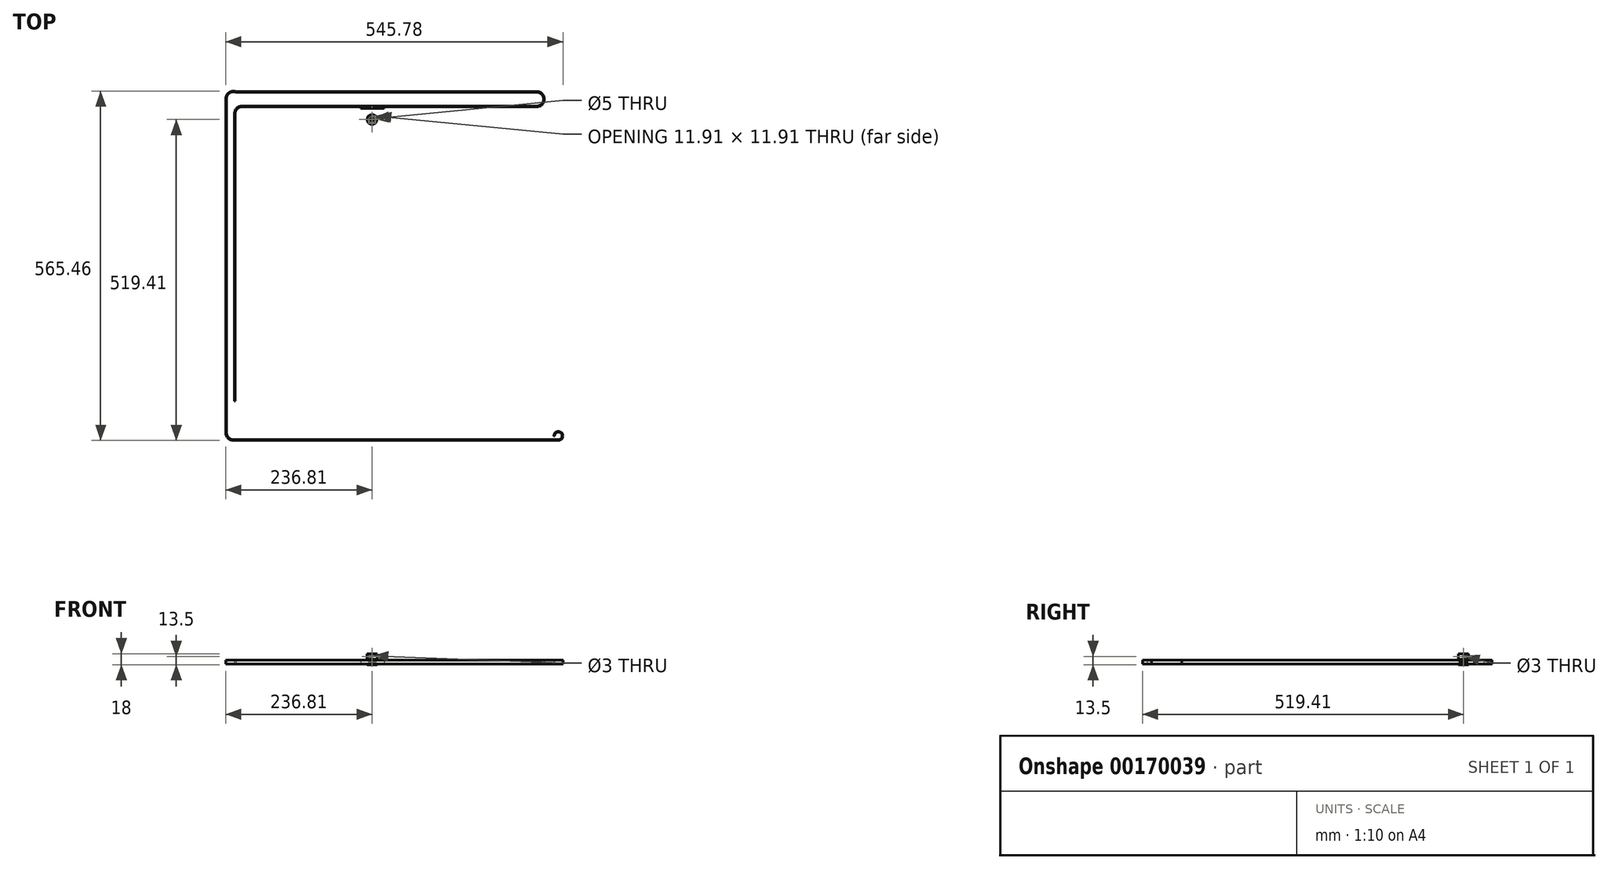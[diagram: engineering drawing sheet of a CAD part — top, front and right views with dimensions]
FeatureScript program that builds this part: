
annotation { "Feature Type Name" : "Feature", "Feature Type Description" : "" }
export const myFeature = defineFeature(function(context is Context, id is Id, definition is map)
    precondition{}
    {
        {
            var Q0;
            Q0=qCreatedBy(makeId("Top.planeOp"),FACE);
            var sketch = newSketch(context, id + "F0", { "sketchPlane" : qUnion([Q0])});
            skLineSegment(sketch, "E0", {"start": v(-19.17, 17.78) * mm, "end": v(-18.17, 17.78) * mm});
            skLineSegment(sketch, "E1", {"start": v(-18.17, 17.78) * mm, "end": v(-18.17, 18.4) * mm});
            skArc(sketch, "E2", {"start": v(-18.67, 18.85) * mm, "mid": v(-18.88, 19.07) * mm, "end": v(-19.17, 19.16) * mm});
            skArc(sketch, "E3", {"start": v(-18.58, 18.54) * mm, "mid": v(-18.61, 18.7) * mm, "end": v(-18.67, 18.85) * mm});
            skArc(sketch, "E4", {"start": v(-18.58, 18.54) * mm, "mid": v(-18.53, 18.44) * mm, "end": v(-18.43, 18.4) * mm});
            skLineSegment(sketch, "E5", {"start": v(-18.43, 18.4) * mm, "end": v(-18.17, 18.4) * mm});
            skArc(sketch, "E6.0.MirrorCS", {"start": v(-19.67, 18.85) * mm, "mid": v(-19.47, 19.07) * mm, "end": v(-19.17, 19.16) * mm});
            skArc(sketch, "E7.0.MirrorCS", {"start": v(-19.76, 18.54) * mm, "mid": v(-19.73, 18.7) * mm, "end": v(-19.67, 18.85) * mm});
            skArc(sketch, "E8.0.MirrorCS", {"start": v(-19.76, 18.54) * mm, "mid": v(-19.81, 18.44) * mm, "end": v(-19.91, 18.4) * mm});
            skLineSegment(sketch, "E9.0.MirrorCS", {"start": v(-19.91, 18.4) * mm, "end": v(-20.17, 18.4) * mm});
            skLineSegment(sketch, "E10.0.MirrorCS", {"start": v(-20.17, 17.78) * mm, "end": v(-20.17, 18.4) * mm});
            skLineSegment(sketch, "E11.0.MirrorCS", {"start": v(-19.17, 17.78) * mm, "end": v(-20.17, 17.78) * mm});
            skLineSegment(sketch, "E12.direction1", {"start": v(-20.17, 17.78) * mm, "end": v(-18.17, 17.78) * mm, "construction": true});
            skLineSegment(sketch, "E13", {"start": v(-20.17, 18.15) * mm, "end": v(-18.17, 18.15) * mm, "construction": true});
            skPoint(sketch, "E14", {"position": v(0, -5.25) * mm});
            skArc(sketch, "E15", {"start": v(0.51, -5.6) * mm, "mid": v(0, -5.25) * mm, "end": v(-0.51, -5.6) * mm});
            skArc(sketch, "E16", {"start": v(-0.51, -5.6) * mm, "mid": v(-0.56, -5.71) * mm, "end": v(-0.59, -5.83) * mm});
            skArc(sketch, "E17", {"start": v(0.59, -5.83) * mm, "mid": v(0.56, -5.71) * mm, "end": v(0.51, -5.6) * mm});
            skArc(sketch, "E18", {"start": v(0.72, -5.96) * mm, "mid": v(0.94, -5.93) * mm, "end": v(1.16, -5.89) * mm});
            skArc(sketch, "E19", {"start": v(0.59, -5.83) * mm, "mid": v(0.66, -5.94) * mm, "end": v(0.8, -5.95) * mm});
            skArc(sketch, "E20", {"start": v(-0.59, -5.83) * mm, "mid": v(-0.66, -5.94) * mm, "end": v(-0.8, -5.95) * mm});
            skArc(sketch, "E21.1.0", {"start": v(2.22, -5.16) * mm, "mid": v(1.62, -5) * mm, "end": v(1.24, -5.48) * mm});
            skPoint(sketch, "E21.1.1", {"position": v(1.62, -5) * mm});
            skArc(sketch, "E21.1.2", {"start": v(1.24, -5.48) * mm, "mid": v(1.23, -5.6) * mm, "end": v(1.24, -5.73) * mm});
            skArc(sketch, "E21.1.3", {"start": v(2.36, -5.37) * mm, "mid": v(2.47, -5.44) * mm, "end": v(2.6, -5.41) * mm});
            skArc(sketch, "E21.1.4", {"start": v(1.24, -5.73) * mm, "mid": v(1.2, -5.85) * mm, "end": v(1.08, -5.9) * mm});
            skArc(sketch, "E21.1.5", {"start": v(2.36, -5.37) * mm, "mid": v(2.3, -5.26) * mm, "end": v(2.22, -5.16) * mm});
            skArc(sketch, "E22.3.2.0", {"start": v(3.7, -4.22) * mm, "mid": v(3.09, -4.25) * mm, "end": v(2.87, -4.83) * mm});
            skPoint(sketch, "E22.4.2.0", {"position": v(3.09, -4.25) * mm});
            skArc(sketch, "E22.5.2.0", {"start": v(2.87, -4.83) * mm, "mid": v(2.9, -4.95) * mm, "end": v(2.95, -5.07) * mm});
            skArc(sketch, "E22.9.2.0", {"start": v(3.9, -4.37) * mm, "mid": v(4.03, -4.41) * mm, "end": v(4.14, -4.35) * mm});
            skArc(sketch, "E22.13.2.0", {"start": v(2.95, -5.07) * mm, "mid": v(2.95, -5.2) * mm, "end": v(2.85, -5.28) * mm});
            skArc(sketch, "E22.17.2.0", {"start": v(3.9, -4.37) * mm, "mid": v(3.81, -4.3) * mm, "end": v(3.7, -4.22) * mm});
            skArc(sketch, "E22.3.3.0", {"start": v(4.83, -2.87) * mm, "mid": v(4.25, -3.09) * mm, "end": v(4.22, -3.7) * mm});
            skPoint(sketch, "E22.4.3.0", {"position": v(4.25, -3.09) * mm});
            skArc(sketch, "E22.5.3.0", {"start": v(4.22, -3.7) * mm, "mid": v(4.3, -3.81) * mm, "end": v(4.37, -3.9) * mm});
            skArc(sketch, "E22.9.3.0", {"start": v(5.07, -2.95) * mm, "mid": v(5.2, -2.95) * mm, "end": v(5.28, -2.85) * mm});
            skArc(sketch, "E22.13.3.0", {"start": v(4.37, -3.9) * mm, "mid": v(4.41, -4.03) * mm, "end": v(4.35, -4.14) * mm});
            skArc(sketch, "E22.17.3.0", {"start": v(5.07, -2.95) * mm, "mid": v(4.95, -2.9) * mm, "end": v(4.83, -2.87) * mm});
            skArc(sketch, "E22.3.4.0", {"start": v(5.48, -1.24) * mm, "mid": v(5, -1.62) * mm, "end": v(5.16, -2.22) * mm});
            skPoint(sketch, "E22.4.4.0", {"position": v(5, -1.62) * mm});
            skArc(sketch, "E22.5.4.0", {"start": v(5.16, -2.22) * mm, "mid": v(5.26, -2.3) * mm, "end": v(5.37, -2.36) * mm});
            skArc(sketch, "E22.9.4.0", {"start": v(5.73, -1.24) * mm, "mid": v(5.85, -1.2) * mm, "end": v(5.9, -1.08) * mm});
            skArc(sketch, "E22.13.4.0", {"start": v(5.37, -2.36) * mm, "mid": v(5.44, -2.47) * mm, "end": v(5.41, -2.6) * mm});
            skArc(sketch, "E22.17.4.0", {"start": v(5.73, -1.24) * mm, "mid": v(5.6, -1.23) * mm, "end": v(5.48, -1.24) * mm});
            skArc(sketch, "E22.3.5.0", {"start": v(5.6, 0.51) * mm, "mid": v(5.25, 0) * mm, "end": v(5.6, -0.51) * mm});
            skPoint(sketch, "E22.4.5.0", {"position": v(5.25, 0) * mm});
            skArc(sketch, "E22.5.5.0", {"start": v(5.6, -0.51) * mm, "mid": v(5.71, -0.56) * mm, "end": v(5.83, -0.59) * mm});
            skArc(sketch, "E22.9.5.0", {"start": v(5.83, 0.59) * mm, "mid": v(5.94, 0.66) * mm, "end": v(5.95, 0.8) * mm});
            skArc(sketch, "E22.13.5.0", {"start": v(5.83, -0.59) * mm, "mid": v(5.94, -0.66) * mm, "end": v(5.95, -0.8) * mm});
            skArc(sketch, "E22.17.5.0", {"start": v(5.83, 0.59) * mm, "mid": v(5.71, 0.56) * mm, "end": v(5.6, 0.51) * mm});
            skArc(sketch, "E22.3.6.0", {"start": v(5.16, 2.22) * mm, "mid": v(5, 1.62) * mm, "end": v(5.48, 1.24) * mm});
            skPoint(sketch, "E22.4.6.0", {"position": v(5, 1.62) * mm});
            skArc(sketch, "E22.5.6.0", {"start": v(5.48, 1.24) * mm, "mid": v(5.6, 1.23) * mm, "end": v(5.73, 1.24) * mm});
            skArc(sketch, "E22.9.6.0", {"start": v(5.37, 2.36) * mm, "mid": v(5.44, 2.47) * mm, "end": v(5.41, 2.6) * mm});
            skArc(sketch, "E22.13.6.0", {"start": v(5.73, 1.24) * mm, "mid": v(5.85, 1.2) * mm, "end": v(5.9, 1.08) * mm});
            skArc(sketch, "E22.17.6.0", {"start": v(5.37, 2.36) * mm, "mid": v(5.26, 2.3) * mm, "end": v(5.16, 2.22) * mm});
            skArc(sketch, "E22.3.7.0", {"start": v(4.22, 3.7) * mm, "mid": v(4.25, 3.09) * mm, "end": v(4.83, 2.87) * mm});
            skPoint(sketch, "E22.4.7.0", {"position": v(4.25, 3.09) * mm});
            skArc(sketch, "E22.5.7.0", {"start": v(4.83, 2.87) * mm, "mid": v(4.95, 2.9) * mm, "end": v(5.07, 2.95) * mm});
            skArc(sketch, "E22.9.7.0", {"start": v(4.37, 3.9) * mm, "mid": v(4.41, 4.03) * mm, "end": v(4.35, 4.14) * mm});
            skArc(sketch, "E22.13.7.0", {"start": v(5.07, 2.95) * mm, "mid": v(5.2, 2.95) * mm, "end": v(5.28, 2.85) * mm});
            skArc(sketch, "E22.17.7.0", {"start": v(4.37, 3.9) * mm, "mid": v(4.3, 3.81) * mm, "end": v(4.22, 3.7) * mm});
            skArc(sketch, "E22.3.8.0", {"start": v(2.87, 4.83) * mm, "mid": v(3.09, 4.25) * mm, "end": v(3.7, 4.22) * mm});
            skPoint(sketch, "E22.4.8.0", {"position": v(3.09, 4.25) * mm});
            skArc(sketch, "E22.5.8.0", {"start": v(3.7, 4.22) * mm, "mid": v(3.81, 4.3) * mm, "end": v(3.9, 4.37) * mm});
            skArc(sketch, "E22.9.8.0", {"start": v(2.95, 5.07) * mm, "mid": v(2.95, 5.2) * mm, "end": v(2.85, 5.28) * mm});
            skArc(sketch, "E22.13.8.0", {"start": v(3.9, 4.37) * mm, "mid": v(4.03, 4.41) * mm, "end": v(4.14, 4.35) * mm});
            skArc(sketch, "E22.17.8.0", {"start": v(2.95, 5.07) * mm, "mid": v(2.9, 4.95) * mm, "end": v(2.87, 4.83) * mm});
            skArc(sketch, "E22.3.9.0", {"start": v(1.24, 5.48) * mm, "mid": v(1.62, 5) * mm, "end": v(2.22, 5.16) * mm});
            skPoint(sketch, "E22.4.9.0", {"position": v(1.62, 5) * mm});
            skArc(sketch, "E22.5.9.0", {"start": v(2.22, 5.16) * mm, "mid": v(2.3, 5.26) * mm, "end": v(2.36, 5.37) * mm});
            skArc(sketch, "E22.9.9.0", {"start": v(1.24, 5.73) * mm, "mid": v(1.2, 5.85) * mm, "end": v(1.08, 5.9) * mm});
            skArc(sketch, "E22.13.9.0", {"start": v(2.36, 5.37) * mm, "mid": v(2.47, 5.44) * mm, "end": v(2.6, 5.41) * mm});
            skArc(sketch, "E22.17.9.0", {"start": v(1.24, 5.73) * mm, "mid": v(1.23, 5.6) * mm, "end": v(1.24, 5.48) * mm});
            skArc(sketch, "E22.3.10.0", {"start": v(-0.51, 5.6) * mm, "mid": v(0, 5.25) * mm, "end": v(0.51, 5.6) * mm});
            skPoint(sketch, "E22.4.10.0", {"position": v(0, 5.25) * mm});
            skArc(sketch, "E22.5.10.0", {"start": v(0.51, 5.6) * mm, "mid": v(0.56, 5.71) * mm, "end": v(0.59, 5.83) * mm});
            skArc(sketch, "E22.9.10.0", {"start": v(-0.59, 5.83) * mm, "mid": v(-0.66, 5.94) * mm, "end": v(-0.8, 5.95) * mm});
            skArc(sketch, "E22.13.10.0", {"start": v(0.59, 5.83) * mm, "mid": v(0.66, 5.94) * mm, "end": v(0.8, 5.95) * mm});
            skArc(sketch, "E22.17.10.0", {"start": v(-0.59, 5.83) * mm, "mid": v(-0.56, 5.71) * mm, "end": v(-0.51, 5.6) * mm});
            skArc(sketch, "E22.3.11.0", {"start": v(-2.22, 5.16) * mm, "mid": v(-1.62, 5) * mm, "end": v(-1.24, 5.48) * mm});
            skPoint(sketch, "E22.4.11.0", {"position": v(-1.62, 5) * mm});
            skArc(sketch, "E22.5.11.0", {"start": v(-1.24, 5.48) * mm, "mid": v(-1.23, 5.6) * mm, "end": v(-1.24, 5.73) * mm});
            skArc(sketch, "E22.9.11.0", {"start": v(-2.36, 5.37) * mm, "mid": v(-2.47, 5.44) * mm, "end": v(-2.6, 5.41) * mm});
            skArc(sketch, "E22.13.11.0", {"start": v(-1.24, 5.73) * mm, "mid": v(-1.2, 5.85) * mm, "end": v(-1.08, 5.9) * mm});
            skArc(sketch, "E22.17.11.0", {"start": v(-2.36, 5.37) * mm, "mid": v(-2.3, 5.26) * mm, "end": v(-2.22, 5.16) * mm});
            skArc(sketch, "E22.3.12.0", {"start": v(-3.7, 4.22) * mm, "mid": v(-3.09, 4.25) * mm, "end": v(-2.87, 4.83) * mm});
            skPoint(sketch, "E22.4.12.0", {"position": v(-3.09, 4.25) * mm});
            skArc(sketch, "E22.5.12.0", {"start": v(-2.87, 4.83) * mm, "mid": v(-2.9, 4.95) * mm, "end": v(-2.95, 5.07) * mm});
            skArc(sketch, "E22.9.12.0", {"start": v(-3.9, 4.37) * mm, "mid": v(-4.03, 4.41) * mm, "end": v(-4.14, 4.35) * mm});
            skArc(sketch, "E22.13.12.0", {"start": v(-2.95, 5.07) * mm, "mid": v(-2.95, 5.2) * mm, "end": v(-2.85, 5.28) * mm});
            skArc(sketch, "E22.17.12.0", {"start": v(-3.9, 4.37) * mm, "mid": v(-3.81, 4.3) * mm, "end": v(-3.7, 4.22) * mm});
            skArc(sketch, "E22.3.13.0", {"start": v(-4.83, 2.87) * mm, "mid": v(-4.25, 3.09) * mm, "end": v(-4.22, 3.7) * mm});
            skPoint(sketch, "E22.4.13.0", {"position": v(-4.25, 3.09) * mm});
            skArc(sketch, "E22.5.13.0", {"start": v(-4.22, 3.7) * mm, "mid": v(-4.3, 3.81) * mm, "end": v(-4.37, 3.9) * mm});
            skArc(sketch, "E22.9.13.0", {"start": v(-5.07, 2.95) * mm, "mid": v(-5.2, 2.95) * mm, "end": v(-5.28, 2.85) * mm});
            skArc(sketch, "E22.13.13.0", {"start": v(-4.37, 3.9) * mm, "mid": v(-4.41, 4.03) * mm, "end": v(-4.35, 4.14) * mm});
            skArc(sketch, "E22.17.13.0", {"start": v(-5.07, 2.95) * mm, "mid": v(-4.95, 2.9) * mm, "end": v(-4.83, 2.87) * mm});
            skArc(sketch, "E22.3.14.0", {"start": v(-5.48, 1.24) * mm, "mid": v(-5, 1.62) * mm, "end": v(-5.16, 2.22) * mm});
            skPoint(sketch, "E22.4.14.0", {"position": v(-5, 1.62) * mm});
            skArc(sketch, "E22.5.14.0", {"start": v(-5.16, 2.22) * mm, "mid": v(-5.26, 2.3) * mm, "end": v(-5.37, 2.36) * mm});
            skArc(sketch, "E22.9.14.0", {"start": v(-5.73, 1.24) * mm, "mid": v(-5.85, 1.2) * mm, "end": v(-5.9, 1.08) * mm});
            skArc(sketch, "E22.13.14.0", {"start": v(-5.37, 2.36) * mm, "mid": v(-5.44, 2.47) * mm, "end": v(-5.41, 2.6) * mm});
            skArc(sketch, "E22.17.14.0", {"start": v(-5.73, 1.24) * mm, "mid": v(-5.6, 1.23) * mm, "end": v(-5.48, 1.24) * mm});
            skArc(sketch, "E22.3.15.0", {"start": v(-5.6, -0.51) * mm, "mid": v(-5.25, 0) * mm, "end": v(-5.6, 0.51) * mm});
            skPoint(sketch, "E22.4.15.0", {"position": v(-5.25, 0) * mm});
            skArc(sketch, "E22.5.15.0", {"start": v(-5.6, 0.51) * mm, "mid": v(-5.71, 0.56) * mm, "end": v(-5.83, 0.59) * mm});
            skArc(sketch, "E22.9.15.0", {"start": v(-5.83, -0.59) * mm, "mid": v(-5.94, -0.66) * mm, "end": v(-5.95, -0.8) * mm});
            skArc(sketch, "E22.13.15.0", {"start": v(-5.83, 0.59) * mm, "mid": v(-5.94, 0.66) * mm, "end": v(-5.95, 0.8) * mm});
            skArc(sketch, "E22.17.15.0", {"start": v(-5.83, -0.59) * mm, "mid": v(-5.71, -0.56) * mm, "end": v(-5.6, -0.51) * mm});
            skArc(sketch, "E22.3.16.0", {"start": v(-5.16, -2.22) * mm, "mid": v(-5, -1.62) * mm, "end": v(-5.48, -1.24) * mm});
            skPoint(sketch, "E22.4.16.0", {"position": v(-5, -1.62) * mm});
            skArc(sketch, "E22.5.16.0", {"start": v(-5.48, -1.24) * mm, "mid": v(-5.6, -1.23) * mm, "end": v(-5.73, -1.24) * mm});
            skArc(sketch, "E22.9.16.0", {"start": v(-5.37, -2.36) * mm, "mid": v(-5.44, -2.47) * mm, "end": v(-5.41, -2.6) * mm});
            skArc(sketch, "E22.13.16.0", {"start": v(-5.73, -1.24) * mm, "mid": v(-5.85, -1.2) * mm, "end": v(-5.9, -1.08) * mm});
            skArc(sketch, "E22.17.16.0", {"start": v(-5.37, -2.36) * mm, "mid": v(-5.26, -2.3) * mm, "end": v(-5.16, -2.22) * mm});
            skArc(sketch, "E22.3.17.0", {"start": v(-4.22, -3.7) * mm, "mid": v(-4.25, -3.09) * mm, "end": v(-4.83, -2.87) * mm});
            skPoint(sketch, "E22.4.17.0", {"position": v(-4.25, -3.09) * mm});
            skArc(sketch, "E22.5.17.0", {"start": v(-4.83, -2.87) * mm, "mid": v(-4.95, -2.9) * mm, "end": v(-5.07, -2.95) * mm});
            skArc(sketch, "E22.9.17.0", {"start": v(-4.37, -3.9) * mm, "mid": v(-4.41, -4.03) * mm, "end": v(-4.35, -4.14) * mm});
            skArc(sketch, "E22.13.17.0", {"start": v(-5.07, -2.95) * mm, "mid": v(-5.2, -2.95) * mm, "end": v(-5.28, -2.85) * mm});
            skArc(sketch, "E22.17.17.0", {"start": v(-4.37, -3.9) * mm, "mid": v(-4.3, -3.81) * mm, "end": v(-4.22, -3.7) * mm});
            skArc(sketch, "E22.3.18.0", {"start": v(-2.87, -4.83) * mm, "mid": v(-3.09, -4.25) * mm, "end": v(-3.7, -4.22) * mm});
            skPoint(sketch, "E22.4.18.0", {"position": v(-3.09, -4.25) * mm});
            skArc(sketch, "E22.5.18.0", {"start": v(-3.7, -4.22) * mm, "mid": v(-3.81, -4.3) * mm, "end": v(-3.9, -4.37) * mm});
            skArc(sketch, "E22.9.18.0", {"start": v(-2.95, -5.07) * mm, "mid": v(-2.95, -5.2) * mm, "end": v(-2.85, -5.28) * mm});
            skArc(sketch, "E22.13.18.0", {"start": v(-3.9, -4.37) * mm, "mid": v(-4.03, -4.41) * mm, "end": v(-4.14, -4.35) * mm});
            skArc(sketch, "E22.17.18.0", {"start": v(-2.95, -5.07) * mm, "mid": v(-2.9, -4.95) * mm, "end": v(-2.87, -4.83) * mm});
            skArc(sketch, "E22.3.19.0", {"start": v(-1.24, -5.48) * mm, "mid": v(-1.62, -5) * mm, "end": v(-2.22, -5.16) * mm});
            skPoint(sketch, "E22.4.19.0", {"position": v(-1.62, -5) * mm});
            skArc(sketch, "E22.5.19.0", {"start": v(-2.22, -5.16) * mm, "mid": v(-2.3, -5.26) * mm, "end": v(-2.36, -5.37) * mm});
            skArc(sketch, "E22.9.19.0", {"start": v(-1.24, -5.73) * mm, "mid": v(-1.2, -5.85) * mm, "end": v(-1.08, -5.9) * mm});
            skArc(sketch, "E22.13.19.0", {"start": v(-2.36, -5.37) * mm, "mid": v(-2.47, -5.44) * mm, "end": v(-2.6, -5.41) * mm});
            skArc(sketch, "E22.17.19.0", {"start": v(-1.24, -5.73) * mm, "mid": v(-1.23, -5.6) * mm, "end": v(-1.24, -5.48) * mm});
            skArc(sketch, "E23.trimOffspring", {"start": v(2.52, -5.44) * mm, "mid": v(2.72, -5.35) * mm, "end": v(2.92, -5.24) * mm});
            skArc(sketch, "E24.trimOffspring", {"start": v(4.08, -4.4) * mm, "mid": v(4.24, -4.24) * mm, "end": v(4.4, -4.08) * mm});
            skArc(sketch, "E25.trimOffspring", {"start": v(5.24, -2.92) * mm, "mid": v(5.33, -2.76) * mm, "end": v(5.41, -2.6) * mm});
            skArc(sketch, "E26.trimOffspring", {"start": v(5.89, -1.16) * mm, "mid": v(5.93, -0.94) * mm, "end": v(5.96, -0.72) * mm});
            skArc(sketch, "E27.trimOffspring", {"start": v(5.44, 2.52) * mm, "mid": v(5.35, 2.72) * mm, "end": v(5.24, 2.92) * mm});
            skArc(sketch, "E28.trimOffspring", {"start": v(4.4, 4.08) * mm, "mid": v(4.24, 4.24) * mm, "end": v(4.08, 4.4) * mm});
            skArc(sketch, "E29.trimOffspring", {"start": v(5.96, 0.72) * mm, "mid": v(5.93, 0.94) * mm, "end": v(5.89, 1.16) * mm});
            skArc(sketch, "E30.trimOffspring", {"start": v(2.92, 5.24) * mm, "mid": v(2.72, 5.35) * mm, "end": v(2.52, 5.44) * mm});
            skArc(sketch, "E31.trimOffspring", {"start": v(1.16, 5.89) * mm, "mid": v(0.94, 5.93) * mm, "end": v(0.72, 5.96) * mm});
            skArc(sketch, "E32.trimOffspring", {"start": v(-0.72, 5.96) * mm, "mid": v(-0.94, 5.93) * mm, "end": v(-1.16, 5.89) * mm});
            skArc(sketch, "E33.trimOffspring", {"start": v(-2.52, 5.44) * mm, "mid": v(-2.72, 5.35) * mm, "end": v(-2.92, 5.24) * mm});
            skArc(sketch, "E34.trimOffspring", {"start": v(-4.08, 4.4) * mm, "mid": v(-4.24, 4.24) * mm, "end": v(-4.4, 4.08) * mm});
            skArc(sketch, "E35.trimOffspring", {"start": v(-5.24, 2.92) * mm, "mid": v(-5.35, 2.72) * mm, "end": v(-5.44, 2.52) * mm});
            skArc(sketch, "E36.trimOffspring", {"start": v(-5.89, 1.16) * mm, "mid": v(-5.93, 0.94) * mm, "end": v(-5.96, 0.72) * mm});
            skArc(sketch, "E37.trimOffspring", {"start": v(-5.96, -0.72) * mm, "mid": v(-5.93, -0.94) * mm, "end": v(-5.89, -1.16) * mm});
            skArc(sketch, "E38.trimOffspring", {"start": v(-5.44, -2.52) * mm, "mid": v(-5.35, -2.72) * mm, "end": v(-5.24, -2.92) * mm});
            skArc(sketch, "E39.trimOffspring", {"start": v(-4.4, -4.08) * mm, "mid": v(-4.24, -4.24) * mm, "end": v(-4.08, -4.4) * mm});
            skArc(sketch, "E40.trimOffspring", {"start": v(-2.92, -5.24) * mm, "mid": v(-2.72, -5.35) * mm, "end": v(-2.52, -5.44) * mm});
            skArc(sketch, "E41.trimOffspring", {"start": v(-1.16, -5.89) * mm, "mid": v(-0.94, -5.93) * mm, "end": v(-0.72, -5.96) * mm});
            skArc(sketch, "E42.1.0.0", {"start": v(-16.67, 18.85) * mm, "mid": v(-16.88, 19.07) * mm, "end": v(-17.17, 19.16) * mm});
            skArc(sketch, "E42.1.0.1", {"start": v(-16.58, 18.54) * mm, "mid": v(-16.61, 18.7) * mm, "end": v(-16.67, 18.85) * mm});
            skArc(sketch, "E42.1.0.2", {"start": v(-16.58, 18.54) * mm, "mid": v(-16.53, 18.44) * mm, "end": v(-16.43, 18.4) * mm});
            skLineSegment(sketch, "E42.1.0.3", {"start": v(-16.43, 18.4) * mm, "end": v(-16.17, 18.4) * mm});
            skArc(sketch, "E42.1.0.4", {"start": v(-17.67, 18.85) * mm, "mid": v(-17.47, 19.07) * mm, "end": v(-17.17, 19.16) * mm});
            skArc(sketch, "E42.1.0.5", {"start": v(-17.76, 18.54) * mm, "mid": v(-17.73, 18.7) * mm, "end": v(-17.67, 18.85) * mm});
            skArc(sketch, "E42.1.0.6", {"start": v(-17.76, 18.54) * mm, "mid": v(-17.81, 18.44) * mm, "end": v(-17.91, 18.4) * mm});
            skLineSegment(sketch, "E42.1.0.7", {"start": v(-17.91, 18.4) * mm, "end": v(-18.17, 18.4) * mm});
            skArc(sketch, "E42.2.0.0", {"start": v(-14.67, 18.85) * mm, "mid": v(-14.88, 19.07) * mm, "end": v(-15.17, 19.16) * mm});
            skArc(sketch, "E42.2.0.1", {"start": v(-14.58, 18.54) * mm, "mid": v(-14.61, 18.7) * mm, "end": v(-14.67, 18.85) * mm});
            skArc(sketch, "E42.2.0.2", {"start": v(-14.58, 18.54) * mm, "mid": v(-14.53, 18.44) * mm, "end": v(-14.43, 18.4) * mm});
            skLineSegment(sketch, "E42.2.0.3", {"start": v(-14.43, 18.4) * mm, "end": v(-14.17, 18.4) * mm});
            skArc(sketch, "E42.2.0.4", {"start": v(-15.67, 18.85) * mm, "mid": v(-15.47, 19.07) * mm, "end": v(-15.17, 19.16) * mm});
            skArc(sketch, "E42.2.0.5", {"start": v(-15.76, 18.54) * mm, "mid": v(-15.73, 18.7) * mm, "end": v(-15.67, 18.85) * mm});
            skArc(sketch, "E42.2.0.6", {"start": v(-15.76, 18.54) * mm, "mid": v(-15.81, 18.44) * mm, "end": v(-15.91, 18.4) * mm});
            skLineSegment(sketch, "E42.2.0.7", {"start": v(-15.91, 18.4) * mm, "end": v(-16.17, 18.4) * mm});
            skArc(sketch, "E42.3.0.0", {"start": v(-12.67, 18.85) * mm, "mid": v(-12.88, 19.07) * mm, "end": v(-13.17, 19.16) * mm});
            skArc(sketch, "E42.3.0.1", {"start": v(-12.58, 18.54) * mm, "mid": v(-12.61, 18.7) * mm, "end": v(-12.67, 18.85) * mm});
            skArc(sketch, "E42.3.0.2", {"start": v(-12.58, 18.54) * mm, "mid": v(-12.53, 18.44) * mm, "end": v(-12.43, 18.4) * mm});
            skLineSegment(sketch, "E42.3.0.3", {"start": v(-12.43, 18.4) * mm, "end": v(-12.17, 18.4) * mm});
            skArc(sketch, "E42.3.0.4", {"start": v(-13.67, 18.85) * mm, "mid": v(-13.47, 19.07) * mm, "end": v(-13.17, 19.16) * mm});
            skArc(sketch, "E42.3.0.5", {"start": v(-13.76, 18.54) * mm, "mid": v(-13.73, 18.7) * mm, "end": v(-13.67, 18.85) * mm});
            skArc(sketch, "E42.3.0.6", {"start": v(-13.76, 18.54) * mm, "mid": v(-13.81, 18.44) * mm, "end": v(-13.91, 18.4) * mm});
            skLineSegment(sketch, "E42.3.0.7", {"start": v(-13.91, 18.4) * mm, "end": v(-14.17, 18.4) * mm});
            skArc(sketch, "E42.4.0.0", {"start": v(-10.67, 18.85) * mm, "mid": v(-10.88, 19.07) * mm, "end": v(-11.17, 19.16) * mm});
            skArc(sketch, "E42.4.0.1", {"start": v(-10.58, 18.54) * mm, "mid": v(-10.61, 18.7) * mm, "end": v(-10.67, 18.85) * mm});
            skArc(sketch, "E42.4.0.2", {"start": v(-10.58, 18.54) * mm, "mid": v(-10.53, 18.44) * mm, "end": v(-10.43, 18.4) * mm});
            skLineSegment(sketch, "E42.4.0.3", {"start": v(-10.43, 18.4) * mm, "end": v(-10.17, 18.4) * mm});
            skArc(sketch, "E42.4.0.4", {"start": v(-11.67, 18.85) * mm, "mid": v(-11.47, 19.07) * mm, "end": v(-11.17, 19.16) * mm});
            skArc(sketch, "E42.4.0.5", {"start": v(-11.76, 18.54) * mm, "mid": v(-11.73, 18.7) * mm, "end": v(-11.67, 18.85) * mm});
            skArc(sketch, "E42.4.0.6", {"start": v(-11.76, 18.54) * mm, "mid": v(-11.81, 18.44) * mm, "end": v(-11.91, 18.4) * mm});
            skLineSegment(sketch, "E42.4.0.7", {"start": v(-11.91, 18.4) * mm, "end": v(-12.17, 18.4) * mm});
            skArc(sketch, "E42.5.0.0", {"start": v(-8.67, 18.85) * mm, "mid": v(-8.88, 19.07) * mm, "end": v(-9.17, 19.16) * mm});
            skArc(sketch, "E42.5.0.1", {"start": v(-8.58, 18.54) * mm, "mid": v(-8.61, 18.7) * mm, "end": v(-8.67, 18.85) * mm});
            skArc(sketch, "E42.5.0.2", {"start": v(-8.58, 18.54) * mm, "mid": v(-8.53, 18.44) * mm, "end": v(-8.43, 18.4) * mm});
            skLineSegment(sketch, "E42.5.0.3", {"start": v(-8.43, 18.4) * mm, "end": v(-8.17, 18.4) * mm});
            skArc(sketch, "E42.5.0.4", {"start": v(-9.67, 18.85) * mm, "mid": v(-9.47, 19.07) * mm, "end": v(-9.17, 19.16) * mm});
            skArc(sketch, "E42.5.0.5", {"start": v(-9.76, 18.54) * mm, "mid": v(-9.73, 18.7) * mm, "end": v(-9.67, 18.85) * mm});
            skArc(sketch, "E42.5.0.6", {"start": v(-9.76, 18.54) * mm, "mid": v(-9.81, 18.44) * mm, "end": v(-9.91, 18.4) * mm});
            skLineSegment(sketch, "E42.5.0.7", {"start": v(-9.91, 18.4) * mm, "end": v(-10.17, 18.4) * mm});
            skArc(sketch, "E42.6.0.0", {"start": v(-6.67, 18.85) * mm, "mid": v(-6.88, 19.07) * mm, "end": v(-7.17, 19.16) * mm});
            skArc(sketch, "E42.6.0.1", {"start": v(-6.58, 18.54) * mm, "mid": v(-6.61, 18.7) * mm, "end": v(-6.67, 18.85) * mm});
            skArc(sketch, "E42.6.0.2", {"start": v(-6.58, 18.54) * mm, "mid": v(-6.53, 18.44) * mm, "end": v(-6.43, 18.4) * mm});
            skLineSegment(sketch, "E42.6.0.3", {"start": v(-6.43, 18.4) * mm, "end": v(-6.17, 18.4) * mm});
            skArc(sketch, "E42.6.0.4", {"start": v(-7.67, 18.85) * mm, "mid": v(-7.47, 19.07) * mm, "end": v(-7.17, 19.16) * mm});
            skArc(sketch, "E42.6.0.5", {"start": v(-7.76, 18.54) * mm, "mid": v(-7.73, 18.7) * mm, "end": v(-7.67, 18.85) * mm});
            skArc(sketch, "E42.6.0.6", {"start": v(-7.76, 18.54) * mm, "mid": v(-7.81, 18.44) * mm, "end": v(-7.91, 18.4) * mm});
            skLineSegment(sketch, "E42.6.0.7", {"start": v(-7.91, 18.4) * mm, "end": v(-8.17, 18.4) * mm});
            skArc(sketch, "E42.7.0.0", {"start": v(-4.67, 18.85) * mm, "mid": v(-4.88, 19.07) * mm, "end": v(-5.17, 19.16) * mm});
            skArc(sketch, "E42.7.0.1", {"start": v(-4.58, 18.54) * mm, "mid": v(-4.61, 18.7) * mm, "end": v(-4.67, 18.85) * mm});
            skArc(sketch, "E42.7.0.2", {"start": v(-4.58, 18.54) * mm, "mid": v(-4.53, 18.44) * mm, "end": v(-4.43, 18.4) * mm});
            skLineSegment(sketch, "E42.7.0.3", {"start": v(-4.43, 18.4) * mm, "end": v(-4.17, 18.4) * mm});
            skArc(sketch, "E42.7.0.4", {"start": v(-5.67, 18.85) * mm, "mid": v(-5.47, 19.07) * mm, "end": v(-5.17, 19.16) * mm});
            skArc(sketch, "E42.7.0.5", {"start": v(-5.76, 18.54) * mm, "mid": v(-5.73, 18.7) * mm, "end": v(-5.67, 18.85) * mm});
            skArc(sketch, "E42.7.0.6", {"start": v(-5.76, 18.54) * mm, "mid": v(-5.81, 18.44) * mm, "end": v(-5.91, 18.4) * mm});
            skLineSegment(sketch, "E42.7.0.7", {"start": v(-5.91, 18.4) * mm, "end": v(-6.17, 18.4) * mm});
            skArc(sketch, "E42.8.0.0", {"start": v(-2.67, 18.85) * mm, "mid": v(-2.88, 19.07) * mm, "end": v(-3.17, 19.16) * mm});
            skArc(sketch, "E42.8.0.1", {"start": v(-2.58, 18.54) * mm, "mid": v(-2.61, 18.7) * mm, "end": v(-2.67, 18.85) * mm});
            skArc(sketch, "E42.8.0.2", {"start": v(-2.58, 18.54) * mm, "mid": v(-2.53, 18.44) * mm, "end": v(-2.43, 18.4) * mm});
            skLineSegment(sketch, "E42.8.0.3", {"start": v(-2.43, 18.4) * mm, "end": v(-2.17, 18.4) * mm});
            skArc(sketch, "E42.8.0.4", {"start": v(-3.67, 18.85) * mm, "mid": v(-3.47, 19.07) * mm, "end": v(-3.17, 19.16) * mm});
            skArc(sketch, "E42.8.0.5", {"start": v(-3.76, 18.54) * mm, "mid": v(-3.73, 18.7) * mm, "end": v(-3.67, 18.85) * mm});
            skArc(sketch, "E42.8.0.6", {"start": v(-3.76, 18.54) * mm, "mid": v(-3.81, 18.44) * mm, "end": v(-3.91, 18.4) * mm});
            skLineSegment(sketch, "E42.8.0.7", {"start": v(-3.91, 18.4) * mm, "end": v(-4.17, 18.4) * mm});
            skArc(sketch, "E42.9.0.0", {"start": v(-0.67, 18.85) * mm, "mid": v(-0.88, 19.07) * mm, "end": v(-1.17, 19.16) * mm});
            skArc(sketch, "E42.9.0.1", {"start": v(-0.58, 18.54) * mm, "mid": v(-0.61, 18.7) * mm, "end": v(-0.67, 18.85) * mm});
            skArc(sketch, "E42.9.0.2", {"start": v(-0.58, 18.54) * mm, "mid": v(-0.53, 18.44) * mm, "end": v(-0.43, 18.4) * mm});
            skLineSegment(sketch, "E42.9.0.3", {"start": v(-0.43, 18.4) * mm, "end": v(-0.17, 18.4) * mm});
            skArc(sketch, "E42.9.0.4", {"start": v(-1.67, 18.85) * mm, "mid": v(-1.47, 19.07) * mm, "end": v(-1.17, 19.16) * mm});
            skArc(sketch, "E42.9.0.5", {"start": v(-1.76, 18.54) * mm, "mid": v(-1.73, 18.7) * mm, "end": v(-1.67, 18.85) * mm});
            skArc(sketch, "E42.9.0.6", {"start": v(-1.76, 18.54) * mm, "mid": v(-1.81, 18.44) * mm, "end": v(-1.91, 18.4) * mm});
            skLineSegment(sketch, "E42.9.0.7", {"start": v(-1.91, 18.4) * mm, "end": v(-2.17, 18.4) * mm});
            skArc(sketch, "E42.10.0.0", {"start": v(1.33, 18.85) * mm, "mid": v(1.12, 19.07) * mm, "end": v(0.83, 19.16) * mm});
            skArc(sketch, "E42.10.0.1", {"start": v(1.42, 18.54) * mm, "mid": v(1.39, 18.7) * mm, "end": v(1.33, 18.85) * mm});
            skArc(sketch, "E42.10.0.2", {"start": v(1.42, 18.54) * mm, "mid": v(1.47, 18.44) * mm, "end": v(1.57, 18.4) * mm});
            skLineSegment(sketch, "E42.10.0.3", {"start": v(1.57, 18.4) * mm, "end": v(1.83, 18.4) * mm});
            skArc(sketch, "E42.10.0.4", {"start": v(0.33, 18.85) * mm, "mid": v(0.53, 19.07) * mm, "end": v(0.83, 19.16) * mm});
            skArc(sketch, "E42.10.0.5", {"start": v(0.24, 18.54) * mm, "mid": v(0.27, 18.7) * mm, "end": v(0.33, 18.85) * mm});
            skArc(sketch, "E42.10.0.6", {"start": v(0.24, 18.54) * mm, "mid": v(0.19, 18.44) * mm, "end": v(0.09, 18.4) * mm});
            skLineSegment(sketch, "E42.10.0.7", {"start": v(0.09, 18.4) * mm, "end": v(-0.17, 18.4) * mm});
            skArc(sketch, "E42.11.0.0", {"start": v(3.33, 18.85) * mm, "mid": v(3.12, 19.07) * mm, "end": v(2.83, 19.16) * mm});
            skArc(sketch, "E42.11.0.1", {"start": v(3.42, 18.54) * mm, "mid": v(3.39, 18.7) * mm, "end": v(3.33, 18.85) * mm});
            skArc(sketch, "E42.11.0.2", {"start": v(3.42, 18.54) * mm, "mid": v(3.47, 18.44) * mm, "end": v(3.57, 18.4) * mm});
            skLineSegment(sketch, "E42.11.0.3", {"start": v(3.57, 18.4) * mm, "end": v(3.83, 18.4) * mm});
            skArc(sketch, "E42.11.0.4", {"start": v(2.33, 18.85) * mm, "mid": v(2.53, 19.07) * mm, "end": v(2.83, 19.16) * mm});
            skArc(sketch, "E42.11.0.5", {"start": v(2.24, 18.54) * mm, "mid": v(2.27, 18.7) * mm, "end": v(2.33, 18.85) * mm});
            skArc(sketch, "E42.11.0.6", {"start": v(2.24, 18.54) * mm, "mid": v(2.19, 18.44) * mm, "end": v(2.09, 18.4) * mm});
            skLineSegment(sketch, "E42.11.0.7", {"start": v(2.09, 18.4) * mm, "end": v(1.83, 18.4) * mm});
            skArc(sketch, "E42.12.0.0", {"start": v(5.33, 18.85) * mm, "mid": v(5.12, 19.07) * mm, "end": v(4.83, 19.16) * mm});
            skArc(sketch, "E42.12.0.1", {"start": v(5.42, 18.54) * mm, "mid": v(5.39, 18.7) * mm, "end": v(5.33, 18.85) * mm});
            skArc(sketch, "E42.12.0.2", {"start": v(5.42, 18.54) * mm, "mid": v(5.47, 18.44) * mm, "end": v(5.57, 18.4) * mm});
            skLineSegment(sketch, "E42.12.0.3", {"start": v(5.57, 18.4) * mm, "end": v(5.83, 18.4) * mm});
            skArc(sketch, "E42.12.0.4", {"start": v(4.33, 18.85) * mm, "mid": v(4.53, 19.07) * mm, "end": v(4.83, 19.16) * mm});
            skArc(sketch, "E42.12.0.5", {"start": v(4.24, 18.54) * mm, "mid": v(4.27, 18.7) * mm, "end": v(4.33, 18.85) * mm});
            skArc(sketch, "E42.12.0.6", {"start": v(4.24, 18.54) * mm, "mid": v(4.19, 18.44) * mm, "end": v(4.09, 18.4) * mm});
            skLineSegment(sketch, "E42.12.0.7", {"start": v(4.09, 18.4) * mm, "end": v(3.83, 18.4) * mm});
            skArc(sketch, "E42.13.0.0", {"start": v(7.33, 18.85) * mm, "mid": v(7.12, 19.07) * mm, "end": v(6.83, 19.16) * mm});
            skArc(sketch, "E42.13.0.1", {"start": v(7.42, 18.54) * mm, "mid": v(7.39, 18.7) * mm, "end": v(7.33, 18.85) * mm});
            skArc(sketch, "E42.13.0.2", {"start": v(7.42, 18.54) * mm, "mid": v(7.47, 18.44) * mm, "end": v(7.57, 18.4) * mm});
            skLineSegment(sketch, "E42.13.0.3", {"start": v(7.57, 18.4) * mm, "end": v(7.83, 18.4) * mm});
            skArc(sketch, "E42.13.0.4", {"start": v(6.33, 18.85) * mm, "mid": v(6.53, 19.07) * mm, "end": v(6.83, 19.16) * mm});
            skArc(sketch, "E42.13.0.5", {"start": v(6.24, 18.54) * mm, "mid": v(6.27, 18.7) * mm, "end": v(6.33, 18.85) * mm});
            skArc(sketch, "E42.13.0.6", {"start": v(6.24, 18.54) * mm, "mid": v(6.19, 18.44) * mm, "end": v(6.09, 18.4) * mm});
            skLineSegment(sketch, "E42.13.0.7", {"start": v(6.09, 18.4) * mm, "end": v(5.83, 18.4) * mm});
            skArc(sketch, "E42.14.0.0", {"start": v(9.33, 18.85) * mm, "mid": v(9.12, 19.07) * mm, "end": v(8.83, 19.16) * mm});
            skArc(sketch, "E42.14.0.1", {"start": v(9.42, 18.54) * mm, "mid": v(9.39, 18.7) * mm, "end": v(9.33, 18.85) * mm});
            skArc(sketch, "E42.14.0.2", {"start": v(9.42, 18.54) * mm, "mid": v(9.47, 18.44) * mm, "end": v(9.57, 18.4) * mm});
            skLineSegment(sketch, "E42.14.0.3", {"start": v(9.57, 18.4) * mm, "end": v(9.83, 18.4) * mm});
            skArc(sketch, "E42.14.0.4", {"start": v(8.33, 18.85) * mm, "mid": v(8.53, 19.07) * mm, "end": v(8.83, 19.16) * mm});
            skArc(sketch, "E42.14.0.5", {"start": v(8.24, 18.54) * mm, "mid": v(8.27, 18.7) * mm, "end": v(8.33, 18.85) * mm});
            skArc(sketch, "E42.14.0.6", {"start": v(8.24, 18.54) * mm, "mid": v(8.19, 18.44) * mm, "end": v(8.09, 18.4) * mm});
            skLineSegment(sketch, "E42.14.0.7", {"start": v(8.09, 18.4) * mm, "end": v(7.83, 18.4) * mm});
            skArc(sketch, "E42.15.0.0", {"start": v(11.33, 18.85) * mm, "mid": v(11.12, 19.07) * mm, "end": v(10.83, 19.16) * mm});
            skArc(sketch, "E42.15.0.1", {"start": v(11.42, 18.54) * mm, "mid": v(11.39, 18.7) * mm, "end": v(11.33, 18.85) * mm});
            skArc(sketch, "E42.15.0.2", {"start": v(11.42, 18.54) * mm, "mid": v(11.47, 18.44) * mm, "end": v(11.57, 18.4) * mm});
            skLineSegment(sketch, "E42.15.0.3", {"start": v(11.57, 18.4) * mm, "end": v(11.83, 18.4) * mm});
            skArc(sketch, "E42.15.0.4", {"start": v(10.33, 18.85) * mm, "mid": v(10.53, 19.07) * mm, "end": v(10.83, 19.16) * mm});
            skArc(sketch, "E42.15.0.5", {"start": v(10.24, 18.54) * mm, "mid": v(10.27, 18.7) * mm, "end": v(10.33, 18.85) * mm});
            skArc(sketch, "E42.15.0.6", {"start": v(10.24, 18.54) * mm, "mid": v(10.19, 18.44) * mm, "end": v(10.09, 18.4) * mm});
            skLineSegment(sketch, "E42.15.0.7", {"start": v(10.09, 18.4) * mm, "end": v(9.83, 18.4) * mm});
            skArc(sketch, "E42.16.0.0", {"start": v(13.33, 18.85) * mm, "mid": v(13.12, 19.07) * mm, "end": v(12.83, 19.16) * mm});
            skArc(sketch, "E42.16.0.1", {"start": v(13.42, 18.54) * mm, "mid": v(13.39, 18.7) * mm, "end": v(13.33, 18.85) * mm});
            skArc(sketch, "E42.16.0.2", {"start": v(13.42, 18.54) * mm, "mid": v(13.47, 18.44) * mm, "end": v(13.57, 18.4) * mm});
            skLineSegment(sketch, "E42.16.0.3", {"start": v(13.57, 18.4) * mm, "end": v(13.83, 18.4) * mm});
            skArc(sketch, "E42.16.0.4", {"start": v(12.33, 18.85) * mm, "mid": v(12.53, 19.07) * mm, "end": v(12.83, 19.16) * mm});
            skArc(sketch, "E42.16.0.5", {"start": v(12.24, 18.54) * mm, "mid": v(12.27, 18.7) * mm, "end": v(12.33, 18.85) * mm});
            skArc(sketch, "E42.16.0.6", {"start": v(12.24, 18.54) * mm, "mid": v(12.19, 18.44) * mm, "end": v(12.09, 18.4) * mm});
            skLineSegment(sketch, "E42.16.0.7", {"start": v(12.09, 18.4) * mm, "end": v(11.83, 18.4) * mm});
            skArc(sketch, "E42.17.0.0", {"start": v(15.33, 18.85) * mm, "mid": v(15.12, 19.07) * mm, "end": v(14.83, 19.16) * mm});
            skArc(sketch, "E42.17.0.1", {"start": v(15.42, 18.54) * mm, "mid": v(15.39, 18.7) * mm, "end": v(15.33, 18.85) * mm});
            skArc(sketch, "E42.17.0.2", {"start": v(15.42, 18.54) * mm, "mid": v(15.47, 18.44) * mm, "end": v(15.57, 18.4) * mm});
            skLineSegment(sketch, "E42.17.0.3", {"start": v(15.57, 18.4) * mm, "end": v(15.83, 18.4) * mm});
            skArc(sketch, "E42.17.0.4", {"start": v(14.33, 18.85) * mm, "mid": v(14.53, 19.07) * mm, "end": v(14.83, 19.16) * mm});
            skArc(sketch, "E42.17.0.5", {"start": v(14.24, 18.54) * mm, "mid": v(14.27, 18.7) * mm, "end": v(14.33, 18.85) * mm});
            skArc(sketch, "E42.17.0.6", {"start": v(14.24, 18.54) * mm, "mid": v(14.19, 18.44) * mm, "end": v(14.09, 18.4) * mm});
            skLineSegment(sketch, "E42.17.0.7", {"start": v(14.09, 18.4) * mm, "end": v(13.83, 18.4) * mm});
            skArc(sketch, "E42.18.0.0", {"start": v(17.33, 18.85) * mm, "mid": v(17.12, 19.07) * mm, "end": v(16.83, 19.16) * mm});
            skArc(sketch, "E42.18.0.1", {"start": v(17.42, 18.54) * mm, "mid": v(17.39, 18.7) * mm, "end": v(17.33, 18.85) * mm});
            skArc(sketch, "E42.18.0.2", {"start": v(17.42, 18.54) * mm, "mid": v(17.47, 18.44) * mm, "end": v(17.57, 18.4) * mm});
            skLineSegment(sketch, "E42.18.0.3", {"start": v(17.57, 18.4) * mm, "end": v(17.83, 18.4) * mm});
            skArc(sketch, "E42.18.0.4", {"start": v(16.33, 18.85) * mm, "mid": v(16.53, 19.07) * mm, "end": v(16.83, 19.16) * mm});
            skArc(sketch, "E42.18.0.5", {"start": v(16.24, 18.54) * mm, "mid": v(16.27, 18.7) * mm, "end": v(16.33, 18.85) * mm});
            skArc(sketch, "E42.18.0.6", {"start": v(16.24, 18.54) * mm, "mid": v(16.19, 18.44) * mm, "end": v(16.09, 18.4) * mm});
            skLineSegment(sketch, "E42.18.0.7", {"start": v(16.09, 18.4) * mm, "end": v(15.83, 18.4) * mm});
            skArc(sketch, "E42.19.0.0", {"start": v(19.33, 18.85) * mm, "mid": v(19.12, 19.07) * mm, "end": v(18.83, 19.16) * mm});
            skArc(sketch, "E42.19.0.1", {"start": v(19.42, 18.54) * mm, "mid": v(19.39, 18.7) * mm, "end": v(19.33, 18.85) * mm});
            skArc(sketch, "E42.19.0.2", {"start": v(19.42, 18.54) * mm, "mid": v(19.47, 18.44) * mm, "end": v(19.57, 18.4) * mm});
            skLineSegment(sketch, "E42.19.0.3", {"start": v(19.57, 18.4) * mm, "end": v(19.83, 18.4) * mm});
            skArc(sketch, "E42.19.0.4", {"start": v(18.33, 18.85) * mm, "mid": v(18.53, 19.07) * mm, "end": v(18.83, 19.16) * mm});
            skArc(sketch, "E42.19.0.5", {"start": v(18.24, 18.54) * mm, "mid": v(18.27, 18.7) * mm, "end": v(18.33, 18.85) * mm});
            skArc(sketch, "E42.19.0.6", {"start": v(18.24, 18.54) * mm, "mid": v(18.19, 18.44) * mm, "end": v(18.09, 18.4) * mm});
            skLineSegment(sketch, "E42.19.0.7", {"start": v(18.09, 18.4) * mm, "end": v(17.83, 18.4) * mm});
            skLineSegment(sketch, "E42.direction1", {"start": v(-20.17, 18.4) * mm, "end": v(-18.17, 18.4) * mm, "construction": true});
            skLineSegment(sketch, "E43", {"start": v(19.83, 18.4) * mm, "end": v(19.83, 17.78) * mm});
            skLineSegment(sketch, "E44", {"start": v(19.83, 17.78) * mm, "end": v(-18.17, 17.78) * mm});
            skLineSegment(sketch, "E45.bottom", {"start": v(-210.4, 20.6) * mm, "end": v(266.6, 20.6) * mm});
            skArc(sketch, "E46", {"start": v(266.6, 21.97) * mm, "mid": v(277.6, 32.97) * mm, "end": v(266.6, 43.97) * mm});
            skLineSegment(sketch, "E47.MirrorCS", {"start": v(-220.4, 43.97) * mm, "end": v(266.6, 43.97) * mm});
            skLineSegment(sketch, "E48.MirrorCS", {"start": v(-220.4, 45.35) * mm, "end": v(266.6, 45.35) * mm});
            skArc(sketch, "E49", {"start": v(-210.4, 20.6) * mm, "mid": v(-218.18, 17.37) * mm, "end": v(-221.4, 9.6) * mm});
            skLineSegment(sketch, "E50", {"start": v(-221.4, 9.6) * mm, "end": v(-221.4, -455.65) * mm});
            skLineSegment(sketch, "E51", {"start": v(-222.79, -455.65) * mm, "end": v(-222.79, 9.6) * mm});
            skArc(sketch, "E52.0", {"start": v(-210.4, 21.97) * mm, "mid": v(-219.16, 18.35) * mm, "end": v(-222.79, 9.6) * mm});
            skLineSegment(sketch, "E53.0", {"start": v(-210.4, 21.97) * mm, "end": v(266.6, 21.97) * mm});
            skArc(sketch, "E54", {"start": v(266.6, 20.6) * mm, "mid": v(278.97, 32.97) * mm, "end": v(266.6, 45.35) * mm});
            skArc(sketch, "E55", {"start": v(-220.4, 43.97) * mm, "mid": v(-230.94, 42.6) * mm, "end": v(-235.4, 32.97) * mm});
            skLineSegment(sketch, "E56", {"start": v(-235.4, 32.97) * mm, "end": v(-235.4, -507.03) * mm});
            skLineSegment(sketch, "E57", {"start": v(-236.79, -507.03) * mm, "end": v(-236.79, 32.97) * mm});
            skArc(sketch, "E58.trimOffspring", {"start": v(-220.4, 45.35) * mm, "mid": v(-231.91, 43.55) * mm, "end": v(-236.79, 32.97) * mm});
            skLineSegment(sketch, "E59.MirrorCS", {"start": v(-224.4, -518.03) * mm, "end": v(291.6, -518.03) * mm});
            skLineSegment(sketch, "E60.MirrorCS", {"start": v(-210.4, -494.65) * mm, "end": v(305.6, -494.65) * mm});
            skLineSegment(sketch, "E61.MirrorCS", {"start": v(-210.4, -496.03) * mm, "end": v(305.6, -496.03) * mm});
            skLineSegment(sketch, "E62.MirrorCS", {"start": v(-224.4, -519.4) * mm, "end": v(291.6, -519.4) * mm});
            skArc(sketch, "E63.MirrorCS", {"start": v(-224.4, -518.03) * mm, "mid": v(-232.18, -514.8) * mm, "end": v(-235.4, -507.03) * mm});
            skArc(sketch, "E64.MirrorCS", {"start": v(-210.4, -496.03) * mm, "mid": v(-219.16, -492.4) * mm, "end": v(-222.79, -483.65) * mm});
            skArc(sketch, "E65.MirrorCS", {"start": v(-224.4, -519.4) * mm, "mid": v(-233.16, -515.78) * mm, "end": v(-236.79, -507.03) * mm});
            skArc(sketch, "E66.MirrorCS", {"start": v(-210.4, -494.65) * mm, "mid": v(-218.18, -491.42) * mm, "end": v(-221.4, -483.65) * mm});
            skLineSegment(sketch, "E67", {"start": v(-222.79, -483.65) * mm, "end": v(-221.4, -483.65) * mm});
            skLineSegment(sketch, "E68", {"start": v(-222.79, -455.65) * mm, "end": v(-221.4, -455.65) * mm});
            skLineSegment(sketch, "E69", {"start": v(291.6, -518.03) * mm, "end": v(301.6, -518.03) * mm});
            skLineSegment(sketch, "E70", {"start": v(301.6, -519.4) * mm, "end": v(291.6, -519.4) * mm});
            skArc(sketch, "E71", {"start": v(301.6, -518.03) * mm, "mid": v(305.84, -507.78) * mm, "end": v(295.6, -512.03) * mm});
            skArc(sketch, "E72.0", {"start": v(301.6, -519.4) * mm, "mid": v(306.81, -506.8) * mm, "end": v(294.21, -512.03) * mm});
            skLineSegment(sketch, "E73", {"start": v(305.6, -494.65) * mm, "end": v(305.6, -496.03) * mm});
            skLineSegment(sketch, "E74", {"start": v(295.6, -512.03) * mm, "end": v(294.21, -512.03) * mm});
            skSolve(sketch);
        }
        {
            var Q0;
            Q0=makeQuery(id+"F0.imprint","IMPRINT",FACE,{"disambiguationData":[TD([[makeQuery(id+"F0.imprint","IMPRINT",EDGE,{"derivedFrom":sQuery(id+"F0.wireOp",EDGE,"E15")}),-1.0]])]});
            extrude(context, id + "F1", {"entities" : qUnion([Q0]), "flatOperationType" : FlatOperationType.REMOVE, "depth" : 7.5 * mm, "offsetDistance" : 25 * mm, "domain" : OperationDomain.MODEL});
        }
        {
            var Q0;
            Q0=makeQuery(id+"F1.opExtrude","CAP_FACE",FACE,{"disambiguationData":[OSD([sQuery(id+"F0.wireOp",EDGE,"E15"),sQuery(id+"F0.wireOp",EDGE,"E16"),sQuery(id+"F0.wireOp",EDGE,"E17"),sQuery(id+"F0.wireOp",EDGE,"E18"),sQuery(id+"F0.wireOp",EDGE,"E19"),sQuery(id+"F0.wireOp",EDGE,"E20"),sQuery(id+"F0.wireOp",EDGE,"E21.1.0"),sQuery(id+"F0.wireOp",EDGE,"E21.1.2"),sQuery(id+"F0.wireOp",EDGE,"E21.1.3"),sQuery(id+"F0.wireOp",EDGE,"E21.1.4"),sQuery(id+"F0.wireOp",EDGE,"E21.1.5"),sQuery(id+"F0.wireOp",EDGE,"E22.3.2.0"),sQuery(id+"F0.wireOp",EDGE,"E22.5.2.0"),sQuery(id+"F0.wireOp",EDGE,"E22.9.2.0"),sQuery(id+"F0.wireOp",EDGE,"E22.13.2.0"),sQuery(id+"F0.wireOp",EDGE,"E22.17.2.0"),sQuery(id+"F0.wireOp",EDGE,"E22.3.3.0"),sQuery(id+"F0.wireOp",EDGE,"E22.5.3.0"),sQuery(id+"F0.wireOp",EDGE,"E22.9.3.0"),sQuery(id+"F0.wireOp",EDGE,"E22.13.3.0"),sQuery(id+"F0.wireOp",EDGE,"E22.17.3.0"),sQuery(id+"F0.wireOp",EDGE,"E22.3.4.0"),sQuery(id+"F0.wireOp",EDGE,"E22.5.4.0"),sQuery(id+"F0.wireOp",EDGE,"E22.9.4.0"),sQuery(id+"F0.wireOp",EDGE,"E22.13.4.0"),sQuery(id+"F0.wireOp",EDGE,"E22.17.4.0"),sQuery(id+"F0.wireOp",EDGE,"E22.3.5.0"),sQuery(id+"F0.wireOp",EDGE,"E22.5.5.0"),sQuery(id+"F0.wireOp",EDGE,"E22.9.5.0"),sQuery(id+"F0.wireOp",EDGE,"E22.13.5.0"),sQuery(id+"F0.wireOp",EDGE,"E22.17.5.0"),sQuery(id+"F0.wireOp",EDGE,"E22.3.6.0"),sQuery(id+"F0.wireOp",EDGE,"E22.5.6.0"),sQuery(id+"F0.wireOp",EDGE,"E22.9.6.0"),sQuery(id+"F0.wireOp",EDGE,"E22.13.6.0"),sQuery(id+"F0.wireOp",EDGE,"E22.17.6.0"),sQuery(id+"F0.wireOp",EDGE,"E22.3.7.0"),sQuery(id+"F0.wireOp",EDGE,"E22.5.7.0"),sQuery(id+"F0.wireOp",EDGE,"E22.9.7.0"),sQuery(id+"F0.wireOp",EDGE,"E22.13.7.0"),sQuery(id+"F0.wireOp",EDGE,"E22.17.7.0"),sQuery(id+"F0.wireOp",EDGE,"E22.3.8.0"),sQuery(id+"F0.wireOp",EDGE,"E22.5.8.0"),sQuery(id+"F0.wireOp",EDGE,"E22.9.8.0"),sQuery(id+"F0.wireOp",EDGE,"E22.13.8.0"),sQuery(id+"F0.wireOp",EDGE,"E22.17.8.0"),sQuery(id+"F0.wireOp",EDGE,"E22.3.9.0"),sQuery(id+"F0.wireOp",EDGE,"E22.5.9.0"),sQuery(id+"F0.wireOp",EDGE,"E22.9.9.0"),sQuery(id+"F0.wireOp",EDGE,"E22.13.9.0"),sQuery(id+"F0.wireOp",EDGE,"E22.17.9.0"),sQuery(id+"F0.wireOp",EDGE,"E22.3.10.0"),sQuery(id+"F0.wireOp",EDGE,"E22.5.10.0"),sQuery(id+"F0.wireOp",EDGE,"E22.9.10.0"),sQuery(id+"F0.wireOp",EDGE,"E22.13.10.0"),sQuery(id+"F0.wireOp",EDGE,"E22.17.10.0"),sQuery(id+"F0.wireOp",EDGE,"E22.3.11.0"),sQuery(id+"F0.wireOp",EDGE,"E22.5.11.0"),sQuery(id+"F0.wireOp",EDGE,"E22.9.11.0"),sQuery(id+"F0.wireOp",EDGE,"E22.13.11.0"),sQuery(id+"F0.wireOp",EDGE,"E22.17.11.0"),sQuery(id+"F0.wireOp",EDGE,"E22.3.12.0"),sQuery(id+"F0.wireOp",EDGE,"E22.5.12.0"),sQuery(id+"F0.wireOp",EDGE,"E22.9.12.0"),sQuery(id+"F0.wireOp",EDGE,"E22.13.12.0"),sQuery(id+"F0.wireOp",EDGE,"E22.17.12.0"),sQuery(id+"F0.wireOp",EDGE,"E22.3.13.0"),sQuery(id+"F0.wireOp",EDGE,"E22.5.13.0"),sQuery(id+"F0.wireOp",EDGE,"E22.9.13.0"),sQuery(id+"F0.wireOp",EDGE,"E22.13.13.0"),sQuery(id+"F0.wireOp",EDGE,"E22.17.13.0"),sQuery(id+"F0.wireOp",EDGE,"E22.3.14.0"),sQuery(id+"F0.wireOp",EDGE,"E22.5.14.0"),sQuery(id+"F0.wireOp",EDGE,"E22.9.14.0"),sQuery(id+"F0.wireOp",EDGE,"E22.13.14.0"),sQuery(id+"F0.wireOp",EDGE,"E22.17.14.0"),sQuery(id+"F0.wireOp",EDGE,"E22.3.15.0"),sQuery(id+"F0.wireOp",EDGE,"E22.5.15.0"),sQuery(id+"F0.wireOp",EDGE,"E22.9.15.0"),sQuery(id+"F0.wireOp",EDGE,"E22.13.15.0"),sQuery(id+"F0.wireOp",EDGE,"E22.17.15.0"),sQuery(id+"F0.wireOp",EDGE,"E22.3.16.0"),sQuery(id+"F0.wireOp",EDGE,"E22.5.16.0"),sQuery(id+"F0.wireOp",EDGE,"E22.9.16.0"),sQuery(id+"F0.wireOp",EDGE,"E22.13.16.0"),sQuery(id+"F0.wireOp",EDGE,"E22.17.16.0"),sQuery(id+"F0.wireOp",EDGE,"E22.3.17.0"),sQuery(id+"F0.wireOp",EDGE,"E22.5.17.0"),sQuery(id+"F0.wireOp",EDGE,"E22.9.17.0"),sQuery(id+"F0.wireOp",EDGE,"E22.13.17.0"),sQuery(id+"F0.wireOp",EDGE,"E22.17.17.0"),sQuery(id+"F0.wireOp",EDGE,"E22.3.18.0"),sQuery(id+"F0.wireOp",EDGE,"E22.5.18.0"),sQuery(id+"F0.wireOp",EDGE,"E22.9.18.0"),sQuery(id+"F0.wireOp",EDGE,"E22.13.18.0"),sQuery(id+"F0.wireOp",EDGE,"E22.17.18.0"),sQuery(id+"F0.wireOp",EDGE,"E22.3.19.0"),sQuery(id+"F0.wireOp",EDGE,"E22.5.19.0"),sQuery(id+"F0.wireOp",EDGE,"E22.9.19.0"),sQuery(id+"F0.wireOp",EDGE,"E22.13.19.0"),sQuery(id+"F0.wireOp",EDGE,"E22.17.19.0"),sQuery(id+"F0.wireOp",EDGE,"E23.trimOffspring"),sQuery(id+"F0.wireOp",EDGE,"E24.trimOffspring"),sQuery(id+"F0.wireOp",EDGE,"E25.trimOffspring"),sQuery(id+"F0.wireOp",EDGE,"E26.trimOffspring"),sQuery(id+"F0.wireOp",EDGE,"E27.trimOffspring"),sQuery(id+"F0.wireOp",EDGE,"E28.trimOffspring"),sQuery(id+"F0.wireOp",EDGE,"E29.trimOffspring"),sQuery(id+"F0.wireOp",EDGE,"E30.trimOffspring"),sQuery(id+"F0.wireOp",EDGE,"E31.trimOffspring"),sQuery(id+"F0.wireOp",EDGE,"E32.trimOffspring"),sQuery(id+"F0.wireOp",EDGE,"E33.trimOffspring"),sQuery(id+"F0.wireOp",EDGE,"E34.trimOffspring"),sQuery(id+"F0.wireOp",EDGE,"E35.trimOffspring"),sQuery(id+"F0.wireOp",EDGE,"E36.trimOffspring"),sQuery(id+"F0.wireOp",EDGE,"E37.trimOffspring"),sQuery(id+"F0.wireOp",EDGE,"E38.trimOffspring"),sQuery(id+"F0.wireOp",EDGE,"E39.trimOffspring"),sQuery(id+"F0.wireOp",EDGE,"E40.trimOffspring"),sQuery(id+"F0.wireOp",EDGE,"E41.trimOffspring")])],"isStart":false});
            var sketch = newSketch(context, id + "F2", { "sketchPlane" : qUnion([Q0])});
            skCircle(sketch, "E75", {"center": v(0, 0) * mm, "radius": 8 * mm});
            skSolve(sketch);
        }
        {
            var Q0;
            Q0=qSketchRegion(id+"F2",true);
            extrude(context, id + "F3", {"entities" : qUnion([Q0]), "operationType" : NewBodyOperationType.ADD, "depth" : 9 * mm});
        }
        {
            var Q0;
            Q0=makeQuery(id+"F1.opExtrude","CAP_FACE",FACE,{"disambiguationData":[OSD([sQuery(id+"F0.wireOp",EDGE,"E15"),sQuery(id+"F0.wireOp",EDGE,"E16"),sQuery(id+"F0.wireOp",EDGE,"E17"),sQuery(id+"F0.wireOp",EDGE,"E18"),sQuery(id+"F0.wireOp",EDGE,"E19"),sQuery(id+"F0.wireOp",EDGE,"E20"),sQuery(id+"F0.wireOp",EDGE,"E21.1.0"),sQuery(id+"F0.wireOp",EDGE,"E21.1.2"),sQuery(id+"F0.wireOp",EDGE,"E21.1.3"),sQuery(id+"F0.wireOp",EDGE,"E21.1.4"),sQuery(id+"F0.wireOp",EDGE,"E21.1.5"),sQuery(id+"F0.wireOp",EDGE,"E22.3.2.0"),sQuery(id+"F0.wireOp",EDGE,"E22.5.2.0"),sQuery(id+"F0.wireOp",EDGE,"E22.9.2.0"),sQuery(id+"F0.wireOp",EDGE,"E22.13.2.0"),sQuery(id+"F0.wireOp",EDGE,"E22.17.2.0"),sQuery(id+"F0.wireOp",EDGE,"E22.3.3.0"),sQuery(id+"F0.wireOp",EDGE,"E22.5.3.0"),sQuery(id+"F0.wireOp",EDGE,"E22.9.3.0"),sQuery(id+"F0.wireOp",EDGE,"E22.13.3.0"),sQuery(id+"F0.wireOp",EDGE,"E22.17.3.0"),sQuery(id+"F0.wireOp",EDGE,"E22.3.4.0"),sQuery(id+"F0.wireOp",EDGE,"E22.5.4.0"),sQuery(id+"F0.wireOp",EDGE,"E22.9.4.0"),sQuery(id+"F0.wireOp",EDGE,"E22.13.4.0"),sQuery(id+"F0.wireOp",EDGE,"E22.17.4.0"),sQuery(id+"F0.wireOp",EDGE,"E22.3.5.0"),sQuery(id+"F0.wireOp",EDGE,"E22.5.5.0"),sQuery(id+"F0.wireOp",EDGE,"E22.9.5.0"),sQuery(id+"F0.wireOp",EDGE,"E22.13.5.0"),sQuery(id+"F0.wireOp",EDGE,"E22.17.5.0"),sQuery(id+"F0.wireOp",EDGE,"E22.3.6.0"),sQuery(id+"F0.wireOp",EDGE,"E22.5.6.0"),sQuery(id+"F0.wireOp",EDGE,"E22.9.6.0"),sQuery(id+"F0.wireOp",EDGE,"E22.13.6.0"),sQuery(id+"F0.wireOp",EDGE,"E22.17.6.0"),sQuery(id+"F0.wireOp",EDGE,"E22.3.7.0"),sQuery(id+"F0.wireOp",EDGE,"E22.5.7.0"),sQuery(id+"F0.wireOp",EDGE,"E22.9.7.0"),sQuery(id+"F0.wireOp",EDGE,"E22.13.7.0"),sQuery(id+"F0.wireOp",EDGE,"E22.17.7.0"),sQuery(id+"F0.wireOp",EDGE,"E22.3.8.0"),sQuery(id+"F0.wireOp",EDGE,"E22.5.8.0"),sQuery(id+"F0.wireOp",EDGE,"E22.9.8.0"),sQuery(id+"F0.wireOp",EDGE,"E22.13.8.0"),sQuery(id+"F0.wireOp",EDGE,"E22.17.8.0"),sQuery(id+"F0.wireOp",EDGE,"E22.3.9.0"),sQuery(id+"F0.wireOp",EDGE,"E22.5.9.0"),sQuery(id+"F0.wireOp",EDGE,"E22.9.9.0"),sQuery(id+"F0.wireOp",EDGE,"E22.13.9.0"),sQuery(id+"F0.wireOp",EDGE,"E22.17.9.0"),sQuery(id+"F0.wireOp",EDGE,"E22.3.10.0"),sQuery(id+"F0.wireOp",EDGE,"E22.5.10.0"),sQuery(id+"F0.wireOp",EDGE,"E22.9.10.0"),sQuery(id+"F0.wireOp",EDGE,"E22.13.10.0"),sQuery(id+"F0.wireOp",EDGE,"E22.17.10.0"),sQuery(id+"F0.wireOp",EDGE,"E22.3.11.0"),sQuery(id+"F0.wireOp",EDGE,"E22.5.11.0"),sQuery(id+"F0.wireOp",EDGE,"E22.9.11.0"),sQuery(id+"F0.wireOp",EDGE,"E22.13.11.0"),sQuery(id+"F0.wireOp",EDGE,"E22.17.11.0"),sQuery(id+"F0.wireOp",EDGE,"E22.3.12.0"),sQuery(id+"F0.wireOp",EDGE,"E22.5.12.0"),sQuery(id+"F0.wireOp",EDGE,"E22.9.12.0"),sQuery(id+"F0.wireOp",EDGE,"E22.13.12.0"),sQuery(id+"F0.wireOp",EDGE,"E22.17.12.0"),sQuery(id+"F0.wireOp",EDGE,"E22.3.13.0"),sQuery(id+"F0.wireOp",EDGE,"E22.5.13.0"),sQuery(id+"F0.wireOp",EDGE,"E22.9.13.0"),sQuery(id+"F0.wireOp",EDGE,"E22.13.13.0"),sQuery(id+"F0.wireOp",EDGE,"E22.17.13.0"),sQuery(id+"F0.wireOp",EDGE,"E22.3.14.0"),sQuery(id+"F0.wireOp",EDGE,"E22.5.14.0"),sQuery(id+"F0.wireOp",EDGE,"E22.9.14.0"),sQuery(id+"F0.wireOp",EDGE,"E22.13.14.0"),sQuery(id+"F0.wireOp",EDGE,"E22.17.14.0"),sQuery(id+"F0.wireOp",EDGE,"E22.3.15.0"),sQuery(id+"F0.wireOp",EDGE,"E22.5.15.0"),sQuery(id+"F0.wireOp",EDGE,"E22.9.15.0"),sQuery(id+"F0.wireOp",EDGE,"E22.13.15.0"),sQuery(id+"F0.wireOp",EDGE,"E22.17.15.0"),sQuery(id+"F0.wireOp",EDGE,"E22.3.16.0"),sQuery(id+"F0.wireOp",EDGE,"E22.5.16.0"),sQuery(id+"F0.wireOp",EDGE,"E22.9.16.0"),sQuery(id+"F0.wireOp",EDGE,"E22.13.16.0"),sQuery(id+"F0.wireOp",EDGE,"E22.17.16.0"),sQuery(id+"F0.wireOp",EDGE,"E22.3.17.0"),sQuery(id+"F0.wireOp",EDGE,"E22.5.17.0"),sQuery(id+"F0.wireOp",EDGE,"E22.9.17.0"),sQuery(id+"F0.wireOp",EDGE,"E22.13.17.0"),sQuery(id+"F0.wireOp",EDGE,"E22.17.17.0"),sQuery(id+"F0.wireOp",EDGE,"E22.3.18.0"),sQuery(id+"F0.wireOp",EDGE,"E22.5.18.0"),sQuery(id+"F0.wireOp",EDGE,"E22.9.18.0"),sQuery(id+"F0.wireOp",EDGE,"E22.13.18.0"),sQuery(id+"F0.wireOp",EDGE,"E22.17.18.0"),sQuery(id+"F0.wireOp",EDGE,"E22.3.19.0"),sQuery(id+"F0.wireOp",EDGE,"E22.5.19.0"),sQuery(id+"F0.wireOp",EDGE,"E22.9.19.0"),sQuery(id+"F0.wireOp",EDGE,"E22.13.19.0"),sQuery(id+"F0.wireOp",EDGE,"E22.17.19.0"),sQuery(id+"F0.wireOp",EDGE,"E23.trimOffspring"),sQuery(id+"F0.wireOp",EDGE,"E24.trimOffspring"),sQuery(id+"F0.wireOp",EDGE,"E25.trimOffspring"),sQuery(id+"F0.wireOp",EDGE,"E26.trimOffspring"),sQuery(id+"F0.wireOp",EDGE,"E27.trimOffspring"),sQuery(id+"F0.wireOp",EDGE,"E28.trimOffspring"),sQuery(id+"F0.wireOp",EDGE,"E29.trimOffspring"),sQuery(id+"F0.wireOp",EDGE,"E30.trimOffspring"),sQuery(id+"F0.wireOp",EDGE,"E31.trimOffspring"),sQuery(id+"F0.wireOp",EDGE,"E32.trimOffspring"),sQuery(id+"F0.wireOp",EDGE,"E33.trimOffspring"),sQuery(id+"F0.wireOp",EDGE,"E34.trimOffspring"),sQuery(id+"F0.wireOp",EDGE,"E35.trimOffspring"),sQuery(id+"F0.wireOp",EDGE,"E36.trimOffspring"),sQuery(id+"F0.wireOp",EDGE,"E37.trimOffspring"),sQuery(id+"F0.wireOp",EDGE,"E38.trimOffspring"),sQuery(id+"F0.wireOp",EDGE,"E39.trimOffspring"),sQuery(id+"F0.wireOp",EDGE,"E40.trimOffspring"),sQuery(id+"F0.wireOp",EDGE,"E41.trimOffspring")])],"isStart":true});
            var sketch = newSketch(context, id + "F4", { "sketchPlane" : qUnion([Q0])});
            skCircle(sketch, "E76", {"center": v(0, 0) * mm, "radius": 8 * mm});
            skSolve(sketch);
        }
        {
            var Q0;
            Q0=qSketchRegion(id+"F4",true);
            extrude(context, id + "F5", {"entities" : qUnion([Q0]), "operationType" : NewBodyOperationType.ADD, "depth" : 1.5 * mm});
        }
        {
            var Q0;
            Q0=makeQuery(id+"F5.opExtrude","CAP_FACE",FACE,{"disambiguationData":[OSD([sQuery(id+"F4.wireOp",EDGE,"E76")])],"isStart":false});
            var sketch = newSketch(context, id + "F6", { "sketchPlane" : qUnion([Q0])});
            skCircle(sketch, "E77", {"center": v(0, 0) * mm, "radius": 2.5 * mm});
            skSolve(sketch);
        }
        {
            var Q0;
            Q0=qSketchRegion(id+"F6",true);
            extrude(context, id + "F7", {"entities" : qUnion([Q0]), "operationType" : NewBodyOperationType.REMOVE, "endBound" : BoundingType.THROUGH_ALL, "oppositeDirection" : true, "depth" : 25 * mm});
        }
        {
            var Q0;
            Q0=qCreatedBy(makeId("Right.planeOp"),FACE);
            var sketch = newSketch(context, id + "F8", { "sketchPlane" : qUnion([Q0])});
            skCircle(sketch, "E78", {"center": v(0, 12) * mm, "radius": 1.5 * mm});
            skSolve(sketch);
        }
        {
            var Q0;
            Q0=qSketchRegion(id+"F8",true);
            extrude(context, id + "F9", {"entities" : qUnion([Q0]), "operationType" : NewBodyOperationType.REMOVE, "endBound" : BoundingType.THROUGH_ALL, "oppositeDirection" : true, "depth" : 25 * mm});
        }
        {
            var Q0;
            Q0=qCreatedBy(makeId("Front.planeOp"),FACE);
            var sketch = newSketch(context, id + "F10", { "sketchPlane" : qUnion([Q0])});
            skCircle(sketch, "E79", {"center": v(0, 12) * mm, "radius": 1.5 * mm});
            skSolve(sketch);
        }
        {
            var Q0;
            Q0=qSketchRegion(id+"F10",true);
            extrude(context, id + "F11", {"entities" : qUnion([Q0]), "operationType" : NewBodyOperationType.REMOVE, "endBound" : BoundingType.THROUGH_ALL, "oppositeDirection" : true, "depth" : 25 * mm});
        }
        {
            var Q0;
            Q0=makeQuery(id+"F0.imprint","IMPRINT",FACE,{"disambiguationData":[TD([[makeQuery(id+"F0.imprint","IMPRINT",EDGE,{"derivedFrom":sQuery(id+"F0.wireOp",EDGE,"E1")}),-1.0]])]});
            var Q1;
            Q1=makeQuery(id+"F0.imprint","IMPRINT",FACE,{"disambiguationData":[TD([[makeQuery(id+"F0.imprint","IMPRINT",EDGE,{"derivedFrom":sQuery(id+"F0.wireOp",EDGE,"E45.bottom")}),1.0]])]});
            extrude(context, id + "F12", {"entities" : qUnion([Q0, Q1]), "depth" : 6 * mm});
        }
    });
